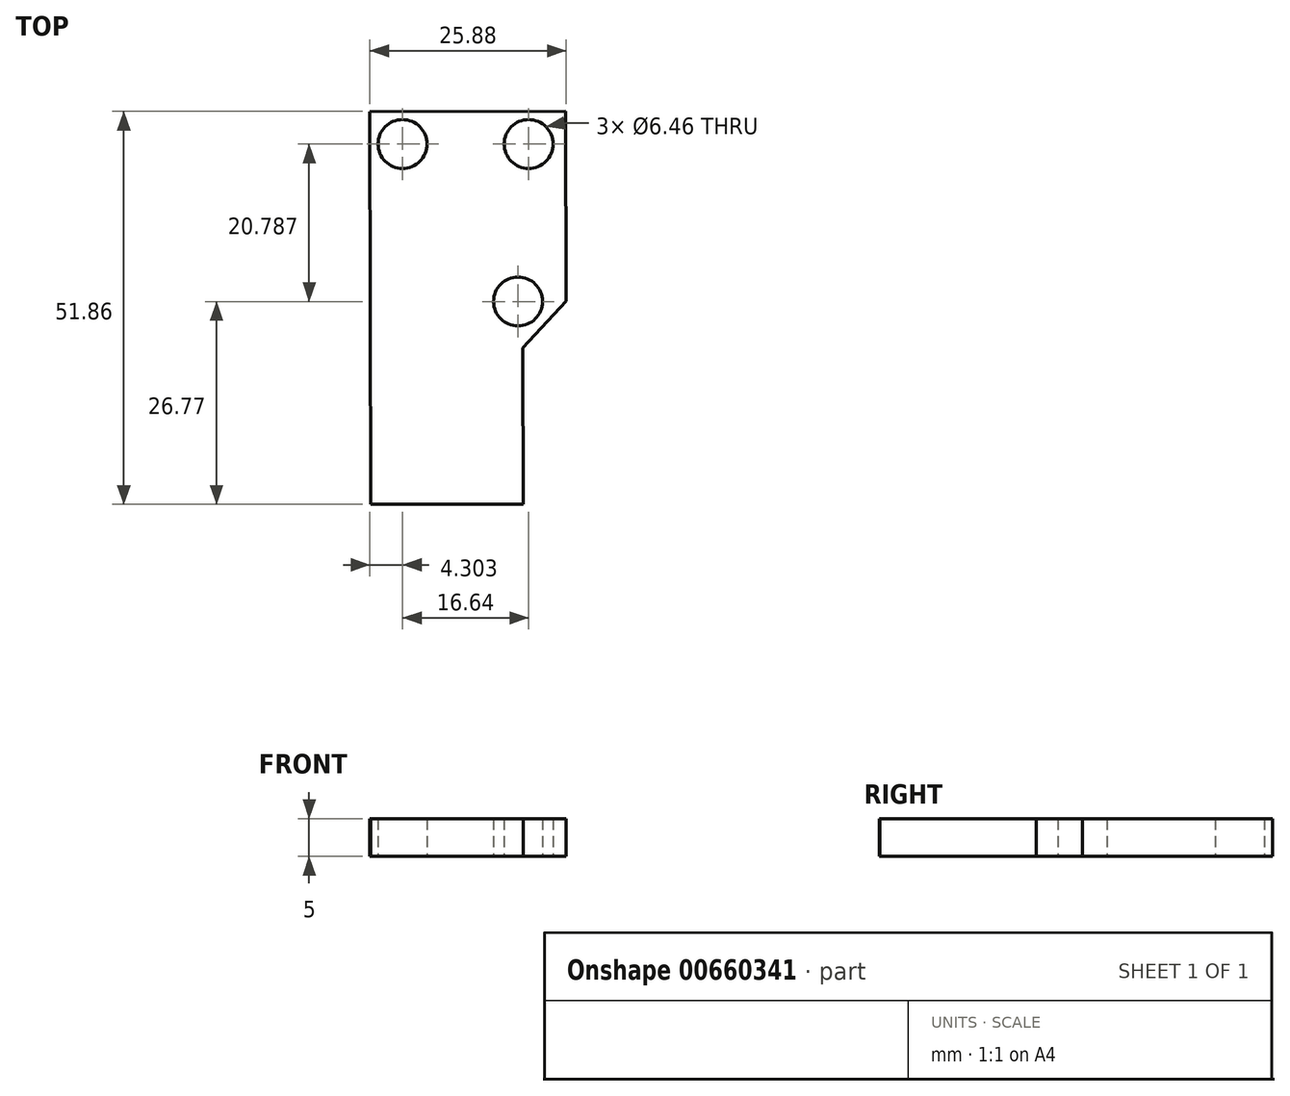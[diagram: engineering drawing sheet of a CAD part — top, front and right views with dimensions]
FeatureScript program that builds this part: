
annotation { "Feature Type Name" : "Feature", "Feature Type Description" : "" }
export const myFeature = defineFeature(function(context is Context, id is Id, definition is map)
    precondition{}
    {
        {
            var Q0;
            Q0=qCreatedBy(makeId("Top.planeOp"),FACE);
            var sketch = newSketch(context, id + "F0", { "sketchPlane" : qUnion([Q0])});
            skPoint(sketch, "E0.startSnap0", {"position": v(2.6, 101.68) * mm});
            skPoint(sketch, "E1.startSnap0", {"position": v(-0.75, 72.9) * mm});
            skLineSegment(sketch, "E2", {"start": v(3.67, 72.74) * mm, "end": v(-9.25, 72.72) * mm});
            skLineSegment(sketch, "E3", {"start": v(-9.25, 72.72) * mm, "end": v(-9.15, 20.9) * mm});
            skLineSegment(sketch, "E4.MirrorCS", {"start": v(3.67, 72.74) * mm, "end": v(16.58, 72.76) * mm});
            skLineSegment(sketch, "E5", {"start": v(-9.15, 20.9) * mm, "end": v(3.84, 20.9) * mm});
            skLineSegment(sketch, "E6", {"start": v(16.58, 72.76) * mm, "end": v(16.63, 47.68) * mm});
            skLineSegment(sketch, "E7", {"start": v(16.63, 47.68) * mm, "end": v(10.91, 41.56) * mm});
            skLineSegment(sketch, "E8", {"start": v(10.91, 41.56) * mm, "end": v(10.95, 20.93) * mm});
            skLineSegment(sketch, "E9", {"start": v(3.84, 20.9) * mm, "end": v(10.95, 20.93) * mm});
            skSolve(sketch);
        }
        {
            var Q0;
            Q0 = qSketchRegion(id + "F0", true);
            extrude(context, id + "F1", {"entities" : qUnion([Q0]), "depth" : 5 * mm, "offsetDistance" : 25 * mm});
        }
        {
            var Q0;
            Q0=makeQuery(id+"F0.imprint","IMPRINT",FACE,{"disambiguationData":[TD([[makeQuery(id+"F0.imprint","IMPRINT",EDGE,{"derivedFrom":sQuery(id+"F0.wireOp",EDGE,"E2")}),1.0]])]});
            extrude(context, id + "F2", {"entities" : qUnion([Q0]), "operationType" : NewBodyOperationType.ADD, "depth" : 4 * mm, "offsetDistance" : 25 * mm});
        }
        {
            var Q0;
            Q0 = qSketchRegion(id + "F0", true);
            extrude(context, id + "F3", {"entities" : qUnion([Q0]), "operationType" : NewBodyOperationType.ADD, "depth" : 4 * mm, "offsetDistance" : 25 * mm});
        }
        {
            var Q0;
            Q0=qCreatedBy(makeId("Top.planeOp"),FACE);
            var sketch = newSketch(context, id + "F4", { "sketchPlane" : qUnion([Q0])});
            skCircle(sketch, "E10", {"center": v(10.3, 47.67) * mm, "radius": 3.23 * mm});
            skCircle(sketch, "E11", {"center": v(11.7, 68.46) * mm, "radius": 3.23 * mm});
            skCircle(sketch, "E12.MirrorC", {"center": v(-4.95, 68.46) * mm, "radius": 3.23 * mm});
            skSolve(sketch);
        }
        {
            var Q0;
            Q0 = qSketchRegion(id + "F4", true);
            extrude(context, id + "F5", {"entities" : qUnion([Q0]), "operationType" : NewBodyOperationType.REMOVE, "depth" : 25 * mm, "offsetDistance" : 25 * mm});
        }
    });
